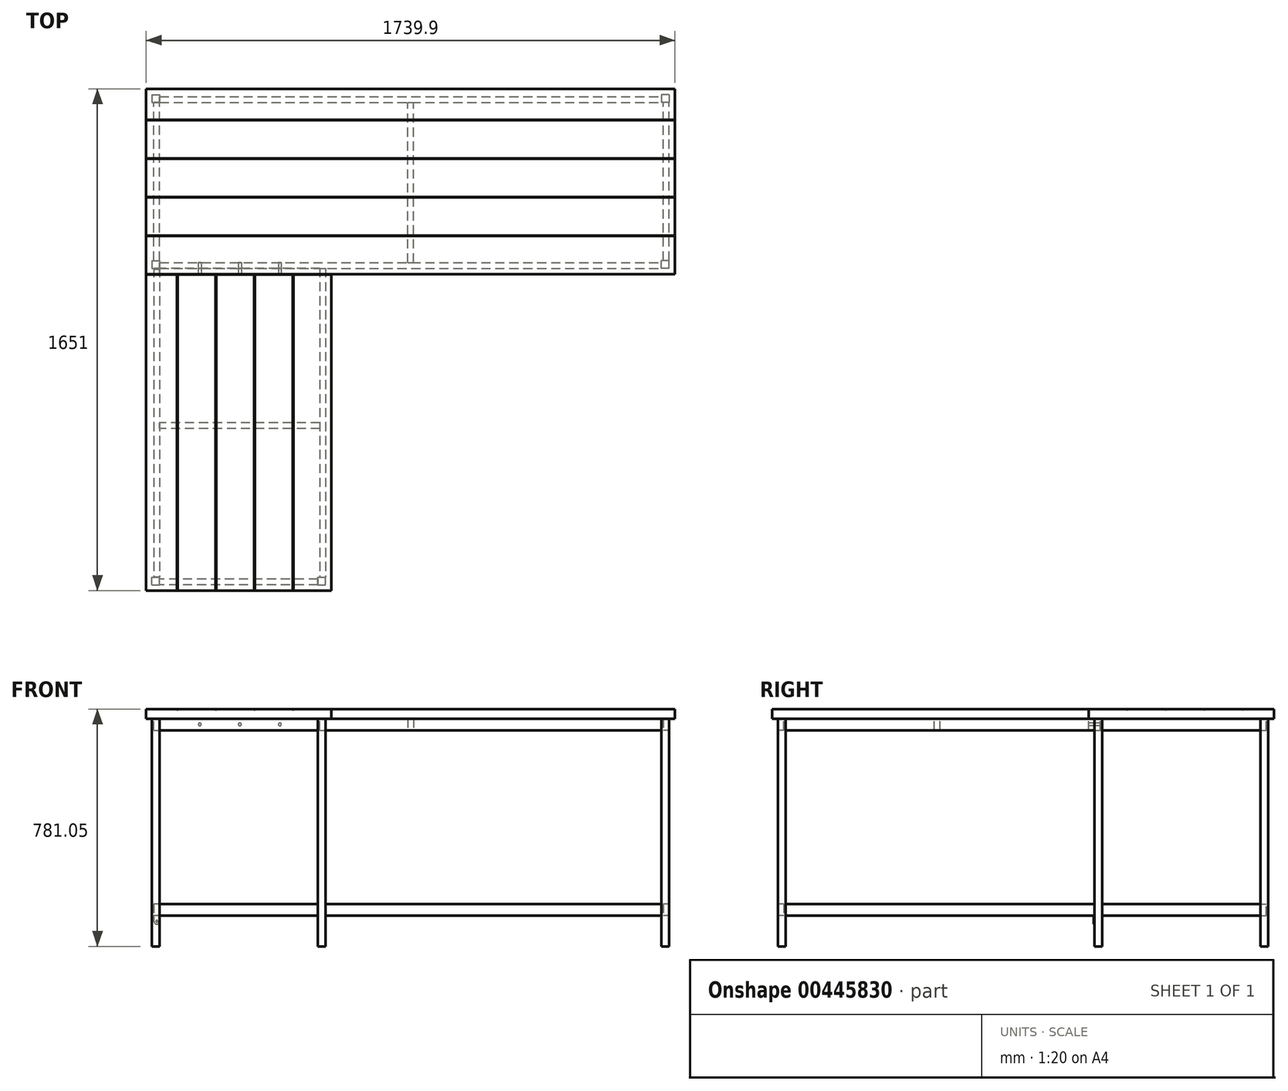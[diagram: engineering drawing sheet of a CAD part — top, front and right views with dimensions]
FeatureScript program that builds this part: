
annotation { "Feature Type Name" : "Feature", "Feature Type Description" : "" }
export const myFeature = defineFeature(function(context is Context, id is Id, definition is map)
    precondition{}
    {
        {
            var Q0;
            Q0=qCreatedBy(makeId("Top.planeOp"),FACE);
            var sketch = newSketch(context, id + "F0", { "sketchPlane" : qUnion([Q0])});
            skLineSegment(sketch, "E0", {"start": v(0, 0) * mm, "end": v(0, 1612.9) * mm, "construction": true});
            skLineSegment(sketch, "E1", {"start": v(0, 1612.9) * mm, "end": v(1701.8, 1612.9) * mm, "construction": true});
            skLineSegment(sketch, "E2.bottom", {"start": v(0, 1612.9) * mm, "end": v(25.4, 1612.9) * mm});
            skLineSegment(sketch, "E2.top", {"start": v(0, 1587.5) * mm, "end": v(25.4, 1587.5) * mm});
            skLineSegment(sketch, "E2.left", {"start": v(0, 1612.9) * mm, "end": v(0, 1587.5) * mm});
            skLineSegment(sketch, "E2.right", {"start": v(25.4, 1612.9) * mm, "end": v(25.4, 1587.5) * mm});
            skLineSegment(sketch, "E3.bottom", {"start": v(0, 1066.8) * mm, "end": v(25.4, 1066.8) * mm});
            skLineSegment(sketch, "E3.top", {"start": v(0, 1041.4) * mm, "end": v(25.4, 1041.4) * mm});
            skLineSegment(sketch, "E3.left", {"start": v(0, 1066.8) * mm, "end": v(0, 1041.4) * mm});
            skLineSegment(sketch, "E3.right", {"start": v(25.4, 1066.8) * mm, "end": v(25.4, 1041.4) * mm});
            skLineSegment(sketch, "E4.bottom", {"start": v(1701.8, 1612.9) * mm, "end": v(1676.4, 1612.9) * mm});
            skLineSegment(sketch, "E4.top", {"start": v(1701.8, 1587.5) * mm, "end": v(1676.4, 1587.5) * mm});
            skLineSegment(sketch, "E4.left", {"start": v(1701.8, 1612.9) * mm, "end": v(1701.8, 1587.5) * mm});
            skLineSegment(sketch, "E4.right", {"start": v(1676.4, 1612.9) * mm, "end": v(1676.4, 1587.5) * mm});
            skLineSegment(sketch, "E5.bottom", {"start": v(1701.8, 1041.4) * mm, "end": v(1676.4, 1041.4) * mm});
            skLineSegment(sketch, "E5.top", {"start": v(1701.8, 1066.8) * mm, "end": v(1676.4, 1066.8) * mm});
            skLineSegment(sketch, "E5.left", {"start": v(1701.8, 1041.4) * mm, "end": v(1701.8, 1066.8) * mm});
            skLineSegment(sketch, "E5.right", {"start": v(1676.4, 1041.4) * mm, "end": v(1676.4, 1066.8) * mm});
            skLineSegment(sketch, "E6.bottom", {"start": v(0, 0) * mm, "end": v(25.4, 0) * mm});
            skLineSegment(sketch, "E6.top", {"start": v(0, 25.4) * mm, "end": v(25.4, 25.4) * mm});
            skLineSegment(sketch, "E6.left", {"start": v(0, 0) * mm, "end": v(0, 25.4) * mm});
            skLineSegment(sketch, "E6.right", {"start": v(25.4, 0) * mm, "end": v(25.4, 25.4) * mm});
            skLineSegment(sketch, "E7.bottom", {"start": v(546.1, 0) * mm, "end": v(571.5, 0) * mm});
            skLineSegment(sketch, "E7.top", {"start": v(546.1, 25.4) * mm, "end": v(571.5, 25.4) * mm});
            skLineSegment(sketch, "E7.left", {"start": v(546.1, 0) * mm, "end": v(546.1, 25.4) * mm});
            skLineSegment(sketch, "E7.right", {"start": v(571.5, 0) * mm, "end": v(571.5, 25.4) * mm});
            skSolve(sketch);
        }
        {
            var Q0;
            Q0 = qSketchRegion(id + "F0", true);
            extrude(context, id + "F1", {"entities" : qUnion([Q0]), "depth" : 749.3 * mm});
        }
        {
            var Q0;
            Q0=makeQuery(id+"F1.opExtrude","SWEPT_FACE",FACE,{"disambiguationData":[OSD([sQuery(id+"F0.wireOp",EDGE,"E5.right")])]});
            var sketch = newSketch(context, id + "F2", { "sketchPlane" : qUnion([Q0])});
            skLineSegment(sketch, "E8.bottom", {"start": v(-1060.45, 749.3) * mm, "end": v(-1041.4, 749.3) * mm});
            skLineSegment(sketch, "E8.top", {"start": v(-1060.45, 711.2) * mm, "end": v(-1041.4, 711.2) * mm});
            skLineSegment(sketch, "E8.left", {"start": v(-1060.45, 749.3) * mm, "end": v(-1060.45, 711.2) * mm});
            skLineSegment(sketch, "E8.right", {"start": v(-1041.4, 749.3) * mm, "end": v(-1041.4, 711.2) * mm});
            skLineSegment(sketch, "E9.bottom", {"start": v(-1606.55, 749.3) * mm, "end": v(-1587.5, 749.3) * mm});
            skLineSegment(sketch, "E9.top", {"start": v(-1606.55, 711.2) * mm, "end": v(-1587.5, 711.2) * mm});
            skLineSegment(sketch, "E9.left", {"start": v(-1606.55, 749.3) * mm, "end": v(-1606.55, 711.2) * mm});
            skLineSegment(sketch, "E9.right", {"start": v(-1587.5, 749.3) * mm, "end": v(-1587.5, 711.2) * mm});
            skSolve(sketch);
        }
        {
            var Q0;
            Q0 = qSketchRegion(id + "F2", true);
            extrude(context, id + "F3", {"entities" : qUnion([Q0]), "endBound" : BoundingType.UP_TO_NEXT, "depth" : 25.4 * mm});
        }
        {
            var Q0;
            Q0=makeQuery(id+"F1.opExtrude","SWEPT_FACE",FACE,{"disambiguationData":[OSD([sQuery(id+"F0.wireOp",EDGE,"E2.top")])]});
            var sketch = newSketch(context, id + "F4", { "sketchPlane" : qUnion([Q0])});
            skLineSegment(sketch, "E10.bottom", {"start": v(25.4, 749.3) * mm, "end": v(6.35, 749.3) * mm});
            skLineSegment(sketch, "E10.top", {"start": v(25.4, 711.2) * mm, "end": v(6.35, 711.2) * mm});
            skLineSegment(sketch, "E10.left", {"start": v(25.4, 749.3) * mm, "end": v(25.4, 711.2) * mm});
            skLineSegment(sketch, "E10.right", {"start": v(6.35, 749.3) * mm, "end": v(6.35, 711.2) * mm});
            skLineSegment(sketch, "E11.bottom", {"start": v(1701.8, 749.3) * mm, "end": v(1682.75, 749.3) * mm});
            skLineSegment(sketch, "E11.top", {"start": v(1701.8, 711.2) * mm, "end": v(1682.75, 711.2) * mm});
            skLineSegment(sketch, "E11.left", {"start": v(1701.8, 749.3) * mm, "end": v(1701.8, 711.2) * mm});
            skLineSegment(sketch, "E11.right", {"start": v(1682.75, 749.3) * mm, "end": v(1682.75, 711.2) * mm});
            skSolve(sketch);
        }
        {
            var Q0;
            Q0 = qSketchRegion(id + "F4", true);
            extrude(context, id + "F5", {"entities" : qUnion([Q0]), "endBound" : BoundingType.UP_TO_NEXT, "depth" : 25.4 * mm});
        }
        {
            var Q0;
            Q0=makeQuery(id+"F1.opExtrude","SWEPT_FACE",FACE,{"disambiguationData":[OSD([sQuery(id+"F0.wireOp",EDGE,"E6.right")])]});
            var sketch = newSketch(context, id + "F6", { "sketchPlane" : qUnion([Q0])});
            skLineSegment(sketch, "E12.bottom", {"start": v(0, 749.3) * mm, "end": v(19.05, 749.3) * mm});
            skLineSegment(sketch, "E12.top", {"start": v(0, 711.2) * mm, "end": v(19.05, 711.2) * mm});
            skLineSegment(sketch, "E12.left", {"start": v(0, 749.3) * mm, "end": v(0, 711.2) * mm});
            skLineSegment(sketch, "E12.right", {"start": v(19.05, 749.3) * mm, "end": v(19.05, 711.2) * mm});
            skSolve(sketch);
        }
        {
            var Q0;
            Q0 = qSketchRegion(id + "F6", true);
            extrude(context, id + "F7", {"entities" : qUnion([Q0]), "endBound" : BoundingType.UP_TO_NEXT, "depth" : 25.4 * mm});
        }
        {
            var Q0;
            Q0=makeQuery(id+"F1.opExtrude","SWEPT_FACE",FACE,{"disambiguationData":[OSD([sQuery(id+"F0.wireOp",EDGE,"E3.top")])]});
            var sketch = newSketch(context, id + "F8", { "sketchPlane" : qUnion([Q0])});
            skLineSegment(sketch, "E13.bottom", {"start": v(25.4, 749.3) * mm, "end": v(6.35, 749.3) * mm});
            skLineSegment(sketch, "E13.top", {"start": v(25.4, 711.2) * mm, "end": v(6.35, 711.2) * mm});
            skLineSegment(sketch, "E13.left", {"start": v(25.4, 749.3) * mm, "end": v(25.4, 711.2) * mm});
            skLineSegment(sketch, "E13.right", {"start": v(6.35, 749.3) * mm, "end": v(6.35, 711.2) * mm});
            skSolve(sketch);
        }
        {
            var Q0;
            Q0 = qSketchRegion(id + "F8", true);
            extrude(context, id + "F9", {"entities" : qUnion([Q0]), "endBound" : BoundingType.UP_TO_NEXT, "depth" : 25.4 * mm});
        }
        {
            var Q0;
            Q0=makeQuery(id+"F1.opExtrude","SWEPT_FACE",FACE,{"disambiguationData":[OSD([sQuery(id+"F0.wireOp",EDGE,"E7.top")])]});
            var sketch = newSketch(context, id + "F10", { "sketchPlane" : qUnion([Q0])});
            skLineSegment(sketch, "E14.bottom", {"start": v(-571.5, 749.3) * mm, "end": v(-552.45, 749.3) * mm});
            skLineSegment(sketch, "E14.top", {"start": v(-571.5, 711.2) * mm, "end": v(-552.45, 711.2) * mm});
            skLineSegment(sketch, "E14.left", {"start": v(-571.5, 749.3) * mm, "end": v(-571.5, 711.2) * mm});
            skLineSegment(sketch, "E14.right", {"start": v(-552.45, 749.3) * mm, "end": v(-552.45, 711.2) * mm});
            skSolve(sketch);
        }
        {
            var Q0;
            Q0 = qSketchRegion(id + "F10", true);
            extrude(context, id + "F11", {"entities" : qUnion([Q0]), "endBound" : BoundingType.UP_TO_NEXT, "depth" : 25.4 * mm});
        }
        {
            var Q0;
            Q0=makeQuery(id+"F9.opExtrude","SWEPT_FACE",FACE,{"disambiguationData":[OSD([sQuery(id+"F8.wireOp",EDGE,"E13.left")])]});
            var sketch = newSketch(context, id + "F12", { "sketchPlane" : qUnion([Q0])});
            skLineSegment(sketch, "E15.bottom", {"start": v(1041.4, 749.3) * mm, "end": v(1022.35, 749.3) * mm});
            skLineSegment(sketch, "E15.top", {"start": v(1041.4, 711.2) * mm, "end": v(1022.35, 711.2) * mm});
            skLineSegment(sketch, "E15.left", {"start": v(1041.4, 749.3) * mm, "end": v(1041.4, 711.2) * mm});
            skLineSegment(sketch, "E15.right", {"start": v(1022.35, 749.3) * mm, "end": v(1022.35, 711.2) * mm});
            skSolve(sketch);
        }
        {
            var Q0;
            Q0 = qSketchRegion(id + "F12", true);
            extrude(context, id + "F13", {"entities" : qUnion([Q0]), "endBound" : BoundingType.UP_TO_NEXT, "depth" : 25.4 * mm});
        }
        {
            var Q0;
            Q0=makeQuery(id+"F13.opExtrude","SWEPT_FACE",FACE,{"disambiguationData":[OSD([sQuery(id+"F12.wireOp",EDGE,"E15.right")])]});
            var sketch = newSketch(context, id + "F14", { "sketchPlane" : qUnion([Q0])});
            skCircle(sketch, "E16", {"center": v(420.69, 730.25) * mm, "radius": 4.76 * mm});
            skCircle(sketch, "E17", {"center": v(288.93, 730.25) * mm, "radius": 4.76 * mm});
            skCircle(sketch, "E18", {"center": v(157.16, 730.25) * mm, "radius": 4.76 * mm});
            skLineSegment(sketch, "E19", {"start": v(25.4, 730.25) * mm, "end": v(157.16, 730.25) * mm, "construction": true});
            skLineSegment(sketch, "E20", {"start": v(288.93, 730.25) * mm, "end": v(157.16, 730.25) * mm, "construction": true});
            skLineSegment(sketch, "E21", {"start": v(288.93, 730.25) * mm, "end": v(420.69, 730.25) * mm, "construction": true});
            skLineSegment(sketch, "E22", {"start": v(420.69, 730.25) * mm, "end": v(552.45, 730.25) * mm, "construction": true});
            skSolve(sketch);
        }
        {
            var Q0;
            Q0 = qSketchRegion(id + "F14", true);
            extrude(context, id + "F15", {"entities" : qUnion([Q0]), "operationType" : NewBodyOperationType.REMOVE, "oppositeDirection" : true, "depth" : 38.1 * mm});
        }
        {
            var Q0;
            Q0=makeQuery(id+"F1.opExtrude","SWEPT_FACE",FACE,{"disambiguationData":[OSD([sQuery(id+"F0.wireOp",EDGE,"E6.right")])]});
            var sketch = newSketch(context, id + "F16", { "sketchPlane" : qUnion([Q0])});
            skLineSegment(sketch, "E23.bottom", {"start": v(0, 101.6) * mm, "end": v(19.05, 101.6) * mm});
            skLineSegment(sketch, "E23.top", {"start": v(0, 139.7) * mm, "end": v(19.05, 139.7) * mm});
            skLineSegment(sketch, "E23.left", {"start": v(0, 101.6) * mm, "end": v(0, 139.7) * mm});
            skLineSegment(sketch, "E23.right", {"start": v(19.05, 101.6) * mm, "end": v(19.05, 139.7) * mm});
            skLineSegment(sketch, "E24.bottom", {"start": v(1587.5, 101.6) * mm, "end": v(1606.55, 101.6) * mm});
            skLineSegment(sketch, "E24.top", {"start": v(1587.5, 139.7) * mm, "end": v(1606.55, 139.7) * mm});
            skLineSegment(sketch, "E24.left", {"start": v(1587.5, 101.6) * mm, "end": v(1587.5, 139.7) * mm});
            skLineSegment(sketch, "E24.right", {"start": v(1606.55, 101.6) * mm, "end": v(1606.55, 139.7) * mm});
            skSolve(sketch);
        }
        {
            var Q0;
            Q0 = qSketchRegion(id + "F16", true);
            extrude(context, id + "F17", {"entities" : qUnion([Q0]), "endBound" : BoundingType.UP_TO_NEXT, "depth" : 25.4 * mm});
        }
        {
            var Q0;
            Q0=makeQuery(id+"F1.opExtrude","SWEPT_FACE",FACE,{"disambiguationData":[OSD([sQuery(id+"F0.wireOp",EDGE,"E4.top")])]});
            var sketch = newSketch(context, id + "F18", { "sketchPlane" : qUnion([Q0])});
            skLineSegment(sketch, "E25.bottom", {"start": v(1701.8, 139.7) * mm, "end": v(1682.75, 139.7) * mm});
            skLineSegment(sketch, "E25.top", {"start": v(1701.8, 101.6) * mm, "end": v(1682.75, 101.6) * mm});
            skLineSegment(sketch, "E25.left", {"start": v(1701.8, 139.7) * mm, "end": v(1701.8, 101.6) * mm});
            skLineSegment(sketch, "E25.right", {"start": v(1682.75, 139.7) * mm, "end": v(1682.75, 101.6) * mm});
            skLineSegment(sketch, "E26.bottom", {"start": v(25.4, 139.7) * mm, "end": v(6.35, 139.7) * mm});
            skLineSegment(sketch, "E26.top", {"start": v(25.4, 101.6) * mm, "end": v(6.35, 101.6) * mm});
            skLineSegment(sketch, "E26.left", {"start": v(25.4, 139.7) * mm, "end": v(25.4, 101.6) * mm});
            skLineSegment(sketch, "E26.right", {"start": v(6.35, 139.7) * mm, "end": v(6.35, 101.6) * mm});
            skSolve(sketch);
        }
        {
            var Q0;
            Q0 = qSketchRegion(id + "F18", true);
            extrude(context, id + "F19", {"entities" : qUnion([Q0]), "endBound" : BoundingType.UP_TO_NEXT, "depth" : 25.4 * mm});
        }
        {
            var Q0;
            Q0=makeQuery(id+"F1.opExtrude","SWEPT_FACE",FACE,{"disambiguationData":[OSD([sQuery(id+"F0.wireOp",EDGE,"E6.top")])]});
            var sketch = newSketch(context, id + "F20", { "sketchPlane" : qUnion([Q0])});
            skLineSegment(sketch, "E27.bottom", {"start": v(-25.4, 139.7) * mm, "end": v(-6.35, 139.7) * mm});
            skLineSegment(sketch, "E27.top", {"start": v(-25.4, 101.6) * mm, "end": v(-6.35, 101.6) * mm});
            skLineSegment(sketch, "E27.left", {"start": v(-25.4, 139.7) * mm, "end": v(-25.4, 101.6) * mm});
            skLineSegment(sketch, "E27.right", {"start": v(-6.35, 139.7) * mm, "end": v(-6.35, 101.6) * mm});
            skSolve(sketch);
        }
        {
            var Q0;
            Q0 = qSketchRegion(id + "F20", true);
            extrude(context, id + "F21", {"entities" : qUnion([Q0]), "endBound" : BoundingType.UP_TO_NEXT, "depth" : 25.4 * mm});
        }
        {
            var Q0;
            Q0=makeQuery(id+"F3.opExtrude","SWEPT_FACE",FACE,{"disambiguationData":[OSD([sQuery(id+"F2.wireOp",EDGE,"E9.right")])]});
            var sketch = newSketch(context, id + "F22", { "sketchPlane" : qUnion([Q0])});
            skLineSegment(sketch, "E28", {"start": v(25.4, 730.25) * mm, "end": v(1676.4, 730.25) * mm, "construction": true});
            skLineSegment(sketch, "E29", {"start": v(850.9, 730.25) * mm, "end": v(850.9, 711.2) * mm, "construction": true});
            skLineSegment(sketch, "E30.bottom", {"start": v(841.37, 749.3) * mm, "end": v(860.42, 749.3) * mm});
            skLineSegment(sketch, "E30.top", {"start": v(841.37, 711.2) * mm, "end": v(860.42, 711.2) * mm});
            skLineSegment(sketch, "E30.left", {"start": v(841.37, 749.3) * mm, "end": v(841.37, 711.2) * mm});
            skLineSegment(sketch, "E30.right", {"start": v(860.42, 749.3) * mm, "end": v(860.42, 711.2) * mm});
            skSolve(sketch);
        }
        {
            var Q0;
            Q0 = qSketchRegion(id + "F22", true);
            extrude(context, id + "F23", {"entities" : qUnion([Q0]), "endBound" : BoundingType.UP_TO_NEXT, "depth" : 25.4 * mm});
        }
        {
            var Q0;
            Q0=makeQuery(id+"F9.opExtrude","SWEPT_FACE",FACE,{"disambiguationData":[OSD([sQuery(id+"F8.wireOp",EDGE,"E13.left")])]});
            var sketch = newSketch(context, id + "F24", { "sketchPlane" : qUnion([Q0])});
            skLineSegment(sketch, "E31", {"start": v(25.4, 730.25) * mm, "end": v(1022.35, 730.25) * mm, "construction": true});
            skLineSegment(sketch, "E32", {"start": v(523.87, 730.25) * mm, "end": v(523.87, 711.2) * mm, "construction": true});
            skLineSegment(sketch, "E33.bottom", {"start": v(514.35, 749.3) * mm, "end": v(533.4, 749.3) * mm});
            skLineSegment(sketch, "E33.top", {"start": v(514.35, 711.2) * mm, "end": v(533.4, 711.2) * mm});
            skLineSegment(sketch, "E33.left", {"start": v(514.35, 749.3) * mm, "end": v(514.35, 711.2) * mm});
            skLineSegment(sketch, "E33.right", {"start": v(533.4, 749.3) * mm, "end": v(533.4, 711.2) * mm});
            skSolve(sketch);
        }
        {
            var Q0;
            Q0 = qSketchRegion(id + "F24", true);
            extrude(context, id + "F25", {"entities" : qUnion([Q0]), "endBound" : BoundingType.UP_TO_NEXT, "depth" : 25.4 * mm});
        }
        {
            var Q0;
            Q0=makeQuery(id+"F1.opExtrude","SWEPT_FACE",FACE,{"disambiguationData":[OSD([sQuery(id+"F0.wireOp",EDGE,"E3.top")])]});
            var sketch = newSketch(context, id + "F26", { "sketchPlane" : qUnion([Q0])});
            skLineSegment(sketch, "E34.bottom", {"start": v(25.4, 101.6) * mm, "end": v(6.35, 101.6) * mm});
            skLineSegment(sketch, "E34.left", {"start": v(25.4, 101.6) * mm, "end": v(25.4, 82.55) * mm});
            skLineSegment(sketch, "E34.right", {"start": v(6.35, 101.6) * mm, "end": v(6.35, 82.55) * mm});
            skArc(sketch, "E35", {"start": v(6.35, 82.55) * mm, "mid": v(15.88, 73.03) * mm, "end": v(25.4, 82.55) * mm});
            skCircle(sketch, "E36", {"center": v(15.88, 82.55) * mm, "radius": 3.18 * mm});
            skSolve(sketch);
        }
        {
            var Q0;
            Q0 = qSketchRegion(id + "F26", true);
            extrude(context, id + "F27", {"entities" : qUnion([Q0]), "depth" : 3.17 * mm});
        }
        {
            var Q0;
            Q0=makeQuery(id+"F1.opExtrude","CAP_FACE",FACE,{"disambiguationData":[OSD([sQuery(id+"F0.wireOp",EDGE,"E3.bottom"),sQuery(id+"F0.wireOp",EDGE,"E3.top"),sQuery(id+"F0.wireOp",EDGE,"E3.left"),sQuery(id+"F0.wireOp",EDGE,"E3.right")])],"isStart":false});
            cPlane(context, id + "F28", {"entities" : qUnion([Q0]), "cplaneType" : CPlaneType.OFFSET, "offset" : 0 * mm, "width" : 152.4 * mm, "height" : 152.4 * mm});
        }
        {
            var Q0;
            Q0=qCreatedBy(id+"F28.planeOp",FACE);
            var sketch = newSketch(context, id + "F29", { "sketchPlane" : qUnion([Q0])});
            skLineSegment(sketch, "E37.bottom", {"start": v(-19.05, 1631.95) * mm, "end": v(1720.85, 1631.95) * mm});
            skLineSegment(sketch, "E37.top", {"start": v(-19.05, 1530.35) * mm, "end": v(1720.85, 1530.35) * mm});
            skLineSegment(sketch, "E37.left", {"start": v(-19.05, 1631.95) * mm, "end": v(-19.05, 1530.35) * mm});
            skLineSegment(sketch, "E37.right", {"start": v(1720.85, 1631.95) * mm, "end": v(1720.85, 1530.35) * mm});
            skLineSegment(sketch, "E38.bottom", {"start": v(1720.85, 1530.35) * mm, "end": v(-19.05, 1530.35) * mm});
            skLineSegment(sketch, "E38.top", {"start": v(1720.85, 1403.35) * mm, "end": v(-19.05, 1403.35) * mm});
            skLineSegment(sketch, "E38.left", {"start": v(1720.85, 1530.35) * mm, "end": v(1720.85, 1403.35) * mm});
            skLineSegment(sketch, "E38.right", {"start": v(-19.05, 1530.35) * mm, "end": v(-19.05, 1403.35) * mm});
            skLineSegment(sketch, "E39.bottom", {"start": v(-19.05, 1403.35) * mm, "end": v(1720.85, 1403.35) * mm});
            skLineSegment(sketch, "E39.top", {"start": v(-19.05, 1276.35) * mm, "end": v(1720.85, 1276.35) * mm});
            skLineSegment(sketch, "E39.left", {"start": v(-19.05, 1403.35) * mm, "end": v(-19.05, 1276.35) * mm});
            skLineSegment(sketch, "E39.right", {"start": v(1720.85, 1403.35) * mm, "end": v(1720.85, 1276.35) * mm});
            skLineSegment(sketch, "E40.bottom", {"start": v(1720.85, 1276.35) * mm, "end": v(-19.05, 1276.35) * mm});
            skLineSegment(sketch, "E40.top", {"start": v(1720.85, 1149.35) * mm, "end": v(-19.05, 1149.35) * mm});
            skLineSegment(sketch, "E40.left", {"start": v(1720.85, 1276.35) * mm, "end": v(1720.85, 1149.35) * mm});
            skLineSegment(sketch, "E40.right", {"start": v(-19.05, 1276.35) * mm, "end": v(-19.05, 1149.35) * mm});
            skLineSegment(sketch, "E41.bottom", {"start": v(-19.05, 1149.35) * mm, "end": v(1720.85, 1149.35) * mm});
            skLineSegment(sketch, "E41.top", {"start": v(-19.05, 1022.35) * mm, "end": v(1720.85, 1022.35) * mm});
            skLineSegment(sketch, "E41.left", {"start": v(-19.05, 1149.35) * mm, "end": v(-19.05, 1022.35) * mm});
            skLineSegment(sketch, "E41.right", {"start": v(1720.85, 1149.35) * mm, "end": v(1720.85, 1022.35) * mm});
            skLineSegment(sketch, "E42.bottom", {"start": v(-19.05, 1022.35) * mm, "end": v(82.55, 1022.35) * mm});
            skLineSegment(sketch, "E42.top", {"start": v(-19.05, -19.05) * mm, "end": v(82.55, -19.05) * mm});
            skLineSegment(sketch, "E42.left", {"start": v(-19.05, 1022.35) * mm, "end": v(-19.05, -19.05) * mm});
            skLineSegment(sketch, "E42.right", {"start": v(82.55, 1022.35) * mm, "end": v(82.55, -19.05) * mm});
            skLineSegment(sketch, "E43.bottom", {"start": v(82.55, -19.05) * mm, "end": v(209.55, -19.05) * mm});
            skLineSegment(sketch, "E43.top", {"start": v(82.55, 1022.35) * mm, "end": v(209.55, 1022.35) * mm});
            skLineSegment(sketch, "E43.left", {"start": v(82.55, -19.05) * mm, "end": v(82.55, 1022.35) * mm});
            skLineSegment(sketch, "E43.right", {"start": v(209.55, -19.05) * mm, "end": v(209.55, 1022.35) * mm});
            skLineSegment(sketch, "E44.bottom", {"start": v(209.55, -19.05) * mm, "end": v(336.55, -19.05) * mm});
            skLineSegment(sketch, "E44.top", {"start": v(209.55, 1022.35) * mm, "end": v(336.55, 1022.35) * mm});
            skLineSegment(sketch, "E44.right", {"start": v(336.55, -19.05) * mm, "end": v(336.55, 1022.35) * mm});
            skLineSegment(sketch, "E45.bottom", {"start": v(336.55, -19.05) * mm, "end": v(463.55, -19.05) * mm});
            skLineSegment(sketch, "E45.top", {"start": v(336.55, 1022.35) * mm, "end": v(463.55, 1022.35) * mm});
            skLineSegment(sketch, "E45.right", {"start": v(463.55, -19.05) * mm, "end": v(463.55, 1022.35) * mm});
            skLineSegment(sketch, "E46.bottom", {"start": v(463.55, -19.05) * mm, "end": v(590.55, -19.05) * mm});
            skLineSegment(sketch, "E46.top", {"start": v(463.55, 1022.35) * mm, "end": v(590.55, 1022.35) * mm});
            skLineSegment(sketch, "E46.right", {"start": v(590.55, -19.05) * mm, "end": v(590.55, 1022.35) * mm});
            skSolve(sketch);
        }
        {
            var Q0;
            Q0 = qSketchRegion(id + "F29", true);
            extrude(context, id + "F30", {"entities" : qUnion([Q0]), "depth" : 31.75 * mm});
        }
        {
            var Q0;
            Q0=makeQuery(id+"F30.opExtrude","CAP_FACE",FACE,{"disambiguationData":[OSD([sQuery(id+"F29.wireOp",EDGE,"E37.bottom"),sQuery(id+"F29.wireOp",EDGE,"E37.left"),sQuery(id+"F29.wireOp",EDGE,"E37.right"),sQuery(id+"F29.wireOp",EDGE,"E38.left"),sQuery(id+"F29.wireOp",EDGE,"E38.right"),sQuery(id+"F29.wireOp",EDGE,"E39.left"),sQuery(id+"F29.wireOp",EDGE,"E39.right"),sQuery(id+"F29.wireOp",EDGE,"E40.left"),sQuery(id+"F29.wireOp",EDGE,"E40.right"),sQuery(id+"F29.wireOp",EDGE,"E41.top"),sQuery(id+"F29.wireOp",EDGE,"E41.left"),sQuery(id+"F29.wireOp",EDGE,"E41.right"),sQuery(id+"F29.wireOp",EDGE,"E42.top"),sQuery(id+"F29.wireOp",EDGE,"E42.left"),sQuery(id+"F29.wireOp",EDGE,"E43.bottom"),sQuery(id+"F29.wireOp",EDGE,"E44.bottom"),sQuery(id+"F29.wireOp",EDGE,"E45.bottom"),sQuery(id+"F29.wireOp",EDGE,"E46.bottom"),sQuery(id+"F29.wireOp",EDGE,"E46.right")])],"isStart":false});
            var sketch = newSketch(context, id + "F31", { "sketchPlane" : qUnion([Q0])});
            skLineSegment(sketch, "E47.0", {"start": v(-19.05, 1631.95) * mm, "end": v(1720.85, 1631.95) * mm, "construction": true});
            skLineSegment(sketch, "E47.1", {"start": v(-19.05, 1530.35) * mm, "end": v(1720.85, 1530.35) * mm, "construction": true});
            skLineSegment(sketch, "E47.2", {"start": v(-19.05, 1631.95) * mm, "end": v(-19.05, 1530.35) * mm, "construction": true});
            skLineSegment(sketch, "E47.3", {"start": v(1720.85, 1631.95) * mm, "end": v(1720.85, 1530.35) * mm, "construction": true});
            skLineSegment(sketch, "E47.4", {"start": v(1720.85, 1530.35) * mm, "end": v(-19.05, 1530.35) * mm, "construction": true});
            skLineSegment(sketch, "E47.5", {"start": v(1720.85, 1403.35) * mm, "end": v(-19.05, 1403.35) * mm, "construction": true});
            skLineSegment(sketch, "E47.6", {"start": v(1720.85, 1530.35) * mm, "end": v(1720.85, 1403.35) * mm, "construction": true});
            skLineSegment(sketch, "E47.7", {"start": v(-19.05, 1530.35) * mm, "end": v(-19.05, 1403.35) * mm, "construction": true});
            skLineSegment(sketch, "E47.8", {"start": v(-19.05, 1403.35) * mm, "end": v(1720.85, 1403.35) * mm, "construction": true});
            skLineSegment(sketch, "E47.9", {"start": v(-19.05, 1276.35) * mm, "end": v(1720.85, 1276.35) * mm, "construction": true});
            skLineSegment(sketch, "E47.10", {"start": v(-19.05, 1403.35) * mm, "end": v(-19.05, 1276.35) * mm, "construction": true});
            skLineSegment(sketch, "E47.11", {"start": v(1720.85, 1403.35) * mm, "end": v(1720.85, 1276.35) * mm, "construction": true});
            skLineSegment(sketch, "E47.12", {"start": v(1720.85, 1276.35) * mm, "end": v(-19.05, 1276.35) * mm, "construction": true});
            skLineSegment(sketch, "E47.13", {"start": v(1720.85, 1149.35) * mm, "end": v(-19.05, 1149.35) * mm, "construction": true});
            skLineSegment(sketch, "E47.14", {"start": v(1720.85, 1276.35) * mm, "end": v(1720.85, 1149.35) * mm, "construction": true});
            skLineSegment(sketch, "E47.15", {"start": v(-19.05, 1276.35) * mm, "end": v(-19.05, 1149.35) * mm, "construction": true});
            skLineSegment(sketch, "E47.16", {"start": v(-19.05, 1149.35) * mm, "end": v(1720.85, 1149.35) * mm, "construction": true});
            skLineSegment(sketch, "E47.17", {"start": v(-19.05, 1022.35) * mm, "end": v(1720.85, 1022.35) * mm, "construction": true});
            skLineSegment(sketch, "E47.18", {"start": v(-19.05, 1149.35) * mm, "end": v(-19.05, 1022.35) * mm, "construction": true});
            skLineSegment(sketch, "E47.19", {"start": v(1720.85, 1149.35) * mm, "end": v(1720.85, 1022.35) * mm, "construction": true});
            skLineSegment(sketch, "E47.20", {"start": v(-19.05, 1022.35) * mm, "end": v(82.55, 1022.35) * mm, "construction": true});
            skLineSegment(sketch, "E47.21", {"start": v(-19.05, -19.05) * mm, "end": v(82.55, -19.05) * mm, "construction": true});
            skLineSegment(sketch, "E47.22", {"start": v(-19.05, 1022.35) * mm, "end": v(-19.05, -19.05) * mm, "construction": true});
            skLineSegment(sketch, "E47.23", {"start": v(82.55, 1022.35) * mm, "end": v(82.55, -19.05) * mm, "construction": true});
            skLineSegment(sketch, "E47.24", {"start": v(82.55, -19.05) * mm, "end": v(209.55, -19.05) * mm, "construction": true});
            skLineSegment(sketch, "E47.25", {"start": v(82.55, 1022.35) * mm, "end": v(209.55, 1022.35) * mm, "construction": true});
            skLineSegment(sketch, "E47.26", {"start": v(82.55, -19.05) * mm, "end": v(82.55, 1022.35) * mm, "construction": true});
            skLineSegment(sketch, "E47.27", {"start": v(209.55, -19.05) * mm, "end": v(209.55, 1022.35) * mm, "construction": true});
            skLineSegment(sketch, "E47.28", {"start": v(209.55, -19.05) * mm, "end": v(336.55, -19.05) * mm, "construction": true});
            skLineSegment(sketch, "E47.29", {"start": v(209.55, 1022.35) * mm, "end": v(336.55, 1022.35) * mm, "construction": true});
            skLineSegment(sketch, "E47.30", {"start": v(209.55, -19.05) * mm, "end": v(209.55, 1022.35) * mm, "construction": true});
            skLineSegment(sketch, "E47.31", {"start": v(336.55, -19.05) * mm, "end": v(336.55, 1022.35) * mm, "construction": true});
            skLineSegment(sketch, "E47.32", {"start": v(336.55, -19.05) * mm, "end": v(463.55, -19.05) * mm, "construction": true});
            skLineSegment(sketch, "E47.33", {"start": v(336.55, 1022.35) * mm, "end": v(463.55, 1022.35) * mm, "construction": true});
            skLineSegment(sketch, "E47.34", {"start": v(336.55, -19.05) * mm, "end": v(336.55, 1022.35) * mm, "construction": true});
            skLineSegment(sketch, "E47.35", {"start": v(463.55, -19.05) * mm, "end": v(463.55, 1022.35) * mm, "construction": true});
            skLineSegment(sketch, "E47.36", {"start": v(463.55, -19.05) * mm, "end": v(590.55, -19.05) * mm, "construction": true});
            skLineSegment(sketch, "E47.37", {"start": v(463.55, 1022.35) * mm, "end": v(590.55, 1022.35) * mm, "construction": true});
            skLineSegment(sketch, "E47.38", {"start": v(463.55, -19.05) * mm, "end": v(463.55, 1022.35) * mm, "construction": true});
            skLineSegment(sketch, "E47.39", {"start": v(590.55, -19.05) * mm, "end": v(590.55, 1022.35) * mm, "construction": true});
            skLineSegment(sketch, "E48.bottom", {"start": v(82.55, -19.05) * mm, "end": v(84.14, -19.05) * mm});
            skLineSegment(sketch, "E48.top", {"start": v(82.55, 1022.35) * mm, "end": v(84.14, 1022.35) * mm});
            skLineSegment(sketch, "E48.left", {"start": v(82.55, -19.05) * mm, "end": v(82.55, 1022.35) * mm});
            skLineSegment(sketch, "E48.right", {"start": v(84.14, -19.05) * mm, "end": v(84.14, 1022.35) * mm});
            skLineSegment(sketch, "E49.bottom", {"start": v(209.55, -19.05) * mm, "end": v(211.14, -19.05) * mm});
            skLineSegment(sketch, "E49.top", {"start": v(209.55, 1022.35) * mm, "end": v(211.14, 1022.35) * mm});
            skLineSegment(sketch, "E49.left", {"start": v(209.55, -19.05) * mm, "end": v(209.55, 1022.35) * mm});
            skLineSegment(sketch, "E49.right", {"start": v(211.14, -19.05) * mm, "end": v(211.14, 1022.35) * mm});
            skLineSegment(sketch, "E50.bottom", {"start": v(336.55, -19.05) * mm, "end": v(338.14, -19.05) * mm});
            skLineSegment(sketch, "E50.top", {"start": v(336.55, 1022.35) * mm, "end": v(338.14, 1022.35) * mm});
            skLineSegment(sketch, "E50.left", {"start": v(336.55, -19.05) * mm, "end": v(336.55, 1022.35) * mm});
            skLineSegment(sketch, "E50.right", {"start": v(338.14, -19.05) * mm, "end": v(338.14, 1022.35) * mm});
            skLineSegment(sketch, "E51.bottom", {"start": v(463.55, -19.05) * mm, "end": v(465.14, -19.05) * mm});
            skLineSegment(sketch, "E51.top", {"start": v(463.55, 1022.35) * mm, "end": v(465.14, 1022.35) * mm});
            skLineSegment(sketch, "E51.left", {"start": v(463.55, -19.05) * mm, "end": v(463.55, 1022.35) * mm});
            skLineSegment(sketch, "E51.right", {"start": v(465.14, -19.05) * mm, "end": v(465.14, 1022.35) * mm});
            skLineSegment(sketch, "E52.bottom", {"start": v(1720.85, 1149.35) * mm, "end": v(-19.05, 1149.35) * mm});
            skLineSegment(sketch, "E52.top", {"start": v(1720.85, 1147.76) * mm, "end": v(-19.05, 1147.76) * mm});
            skLineSegment(sketch, "E52.left", {"start": v(1720.85, 1149.35) * mm, "end": v(1720.85, 1147.76) * mm});
            skLineSegment(sketch, "E52.right", {"start": v(-19.05, 1149.35) * mm, "end": v(-19.05, 1147.76) * mm});
            skLineSegment(sketch, "E53.bottom", {"start": v(1720.85, 1276.35) * mm, "end": v(-19.05, 1276.35) * mm});
            skLineSegment(sketch, "E53.top", {"start": v(1720.85, 1274.76) * mm, "end": v(-19.05, 1274.76) * mm});
            skLineSegment(sketch, "E53.left", {"start": v(1720.85, 1276.35) * mm, "end": v(1720.85, 1274.76) * mm});
            skLineSegment(sketch, "E53.right", {"start": v(-19.05, 1276.35) * mm, "end": v(-19.05, 1274.76) * mm});
            skLineSegment(sketch, "E54.bottom", {"start": v(1720.85, 1403.35) * mm, "end": v(-19.05, 1403.35) * mm});
            skLineSegment(sketch, "E54.top", {"start": v(1720.85, 1401.76) * mm, "end": v(-19.05, 1401.76) * mm});
            skLineSegment(sketch, "E54.left", {"start": v(1720.85, 1403.35) * mm, "end": v(1720.85, 1401.76) * mm});
            skLineSegment(sketch, "E54.right", {"start": v(-19.05, 1403.35) * mm, "end": v(-19.05, 1401.76) * mm});
            skLineSegment(sketch, "E55.bottom", {"start": v(1720.85, 1530.35) * mm, "end": v(-19.05, 1530.35) * mm});
            skLineSegment(sketch, "E55.top", {"start": v(1720.85, 1528.76) * mm, "end": v(-19.05, 1528.76) * mm});
            skLineSegment(sketch, "E55.left", {"start": v(1720.85, 1530.35) * mm, "end": v(1720.85, 1528.76) * mm});
            skLineSegment(sketch, "E55.right", {"start": v(-19.05, 1530.35) * mm, "end": v(-19.05, 1528.76) * mm});
            skLineSegment(sketch, "E56.bottom", {"start": v(-19.05, 1022.35) * mm, "end": v(590.55, 1022.35) * mm});
            skLineSegment(sketch, "E56.top", {"start": v(-19.05, 1020.76) * mm, "end": v(590.55, 1020.76) * mm});
            skLineSegment(sketch, "E56.left", {"start": v(-19.05, 1022.35) * mm, "end": v(-19.05, 1020.76) * mm});
            skLineSegment(sketch, "E56.right", {"start": v(590.55, 1022.35) * mm, "end": v(590.55, 1020.76) * mm});
            skSolve(sketch);
        }
        {
            var Q0;
            Q0 = qSketchRegion(id + "F31", true);
            extrude(context, id + "F32", {"entities" : qUnion([Q0]), "operationType" : NewBodyOperationType.REMOVE, "oppositeDirection" : true, "depth" : 1.59 * mm});
        }
    });
